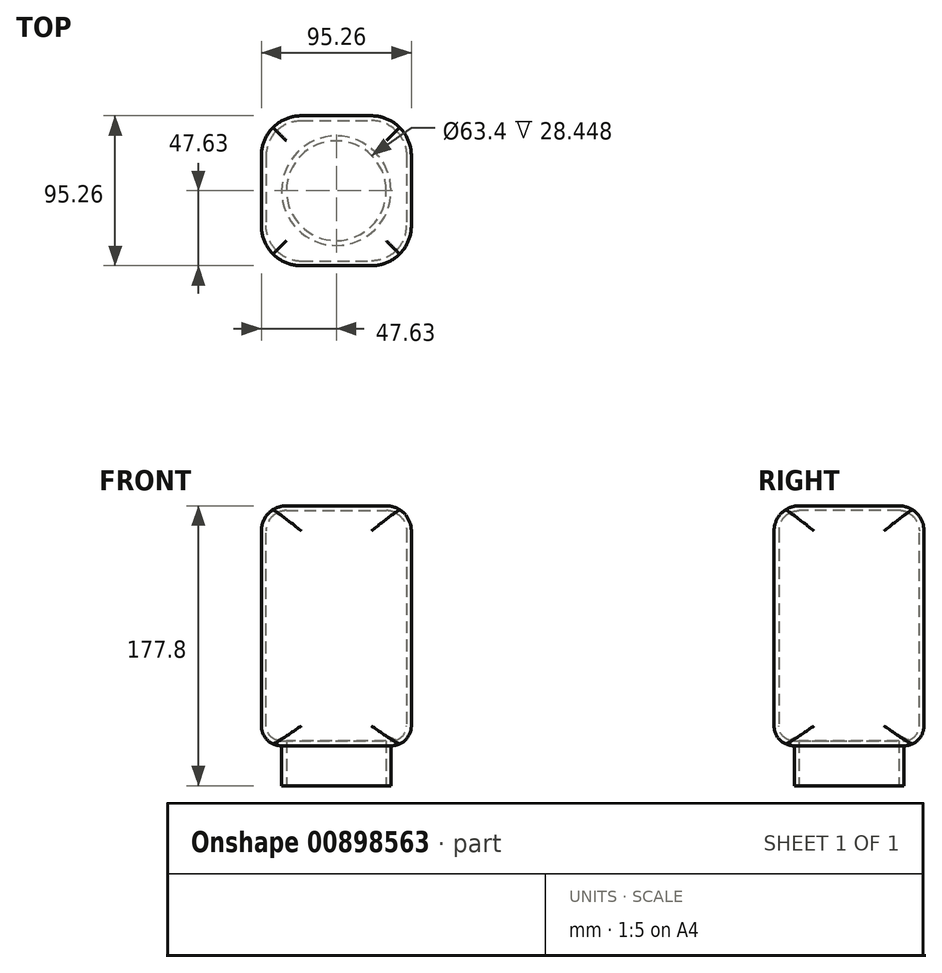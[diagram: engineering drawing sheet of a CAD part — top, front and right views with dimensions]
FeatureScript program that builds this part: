
annotation { "Feature Type Name" : "Feature", "Feature Type Description" : "" }
export const myFeature = defineFeature(function(context is Context, id is Id, definition is map)
    precondition{}
    {
        {
            var Q0;
            Q0=qCreatedBy(makeId("Front.planeOp"),FACE);
            var sketch = newSketch(context, id + "F0", { "sketchPlane" : qUnion([Q0])});
            skLineSegment(sketch, "E0", {"start": v(0, 0) * mm, "end": v(0, 110.8) * mm, "construction": true});
            skLineSegment(sketch, "E1", {"start": v(0, 0) * mm, "end": v(-34.75, 0) * mm});
            skLineSegment(sketch, "E2", {"start": v(-34.75, 0) * mm, "end": v(-34.75, -25.4) * mm});
            skLineSegment(sketch, "E3", {"start": v(-34.75, -25.4) * mm, "end": v(0, -25.4) * mm});
            skLineSegment(sketch, "E4", {"start": v(0, -25.4) * mm, "end": v(0, 0) * mm});
            skSolve(sketch);
        }
        {
            var Q0;
            Q0=makeQuery(id+"F0.imprint","IMPRINT",FACE,{"disambiguationData":[TD([[makeQuery(id+"F0.imprint","IMPRINT",EDGE,{"derivedFrom":sQuery(id+"F0.wireOp",EDGE,"E1")}),1.0]])]});
            var Q1;
            Q1=sQuery(id+"F0.wireOp",EDGE,"E0");
            revolve(context, id + "F1", {"surfaceOperationType" : NewSurfaceOperationType.NEW, "entities" : qUnion([Q0]), "axis" : qUnion([Q1]), "revolveType" : RevolveType.FULL});
        }
        {
            var Q0;
            Q0=qCreatedBy(makeId("Top.planeOp"),FACE);
            var sketch = newSketch(context, id + "F2", { "sketchPlane" : qUnion([Q0])});
            skLineSegment(sketch, "E5", {"start": v(-22.23, 47.63) * mm, "end": v(22.23, 47.63) * mm});
            skLineSegment(sketch, "E6", {"start": v(47.63, 22.23) * mm, "end": v(47.63, -22.23) * mm});
            skLineSegment(sketch, "E7", {"start": v(22.23, -47.63) * mm, "end": v(-22.22, -47.63) * mm});
            skLineSegment(sketch, "E8", {"start": v(-47.62, -22.23) * mm, "end": v(-47.62, 22.23) * mm});
            skPoint(sketch, "E9.visualSharp", {"position": v(-47.62, 47.63) * mm});
            skArc(sketch, "E9.filletArc", {"start": v(-22.23, 47.63) * mm, "mid": v(-40.19, 40.19) * mm, "end": v(-47.63, 22.23) * mm});
            skPoint(sketch, "E10.visualSharp", {"position": v(47.63, -47.63) * mm});
            skArc(sketch, "E10.filletArc", {"start": v(22.23, -47.63) * mm, "mid": v(40.19, -40.19) * mm, "end": v(47.63, -22.23) * mm});
            skPoint(sketch, "E11.visualSharp", {"position": v(47.62, 47.63) * mm});
            skArc(sketch, "E11.filletArc", {"start": v(47.62, 22.23) * mm, "mid": v(40.19, 40.19) * mm, "end": v(22.23, 47.62) * mm});
            skPoint(sketch, "E12.visualSharp", {"position": v(-47.62, -47.63) * mm});
            skArc(sketch, "E12.filletArc", {"start": v(-47.62, -22.23) * mm, "mid": v(-40.19, -40.19) * mm, "end": v(-22.22, -47.63) * mm});
            skSolve(sketch);
        }
        {
            var Q0;
            Q0=makeQuery(id+"F2.imprint","IMPRINT",FACE,{"disambiguationData":[TD([[makeQuery(id+"F2.imprint","IMPRINT",EDGE,{"derivedFrom":sQuery(id+"F2.wireOp",EDGE,"E5")}),-1.0]])]});
            extrude(context, id + "F3", {"entities" : qUnion([Q0]), "operationType" : NewBodyOperationType.ADD, "depth" : 152.4 * mm, "offsetDistance" : 25.4 * mm});
        }
        {
            var Q0;
            Q0=qCreatedBy(makeId("Front.planeOp"),FACE);
            var sketch = newSketch(context, id + "F4", { "sketchPlane" : qUnion([Q0])});
            skPoint(sketch, "E13.0", {"position": v(-47.62, 0) * mm});
            skPoint(sketch, "E14.0", {"position": v(-47.62, 152.4) * mm});
            skPoint(sketch, "E15.0", {"position": v(47.63, 0) * mm});
            skPoint(sketch, "E16.0", {"position": v(47.63, 152.4) * mm});
            skLineSegment(sketch, "E17", {"start": v(-47.62, 152.4) * mm, "end": v(-47.62, 141.05) * mm});
            skLineSegment(sketch, "E18", {"start": v(-47.62, 0) * mm, "end": v(-47.62, 12.7) * mm});
            skLineSegment(sketch, "E19", {"start": v(-47.62, 152.4) * mm, "end": v(-31.75, 152.4) * mm});
            skArc(sketch, "E20", {"start": v(-31.75, 152.4) * mm, "mid": v(-42.98, 147.75) * mm, "end": v(-47.63, 136.53) * mm});
            skArc(sketch, "E21", {"start": v(47.62, 136.53) * mm, "mid": v(42.98, 147.75) * mm, "end": v(31.75, 152.4) * mm});
            skArc(sketch, "E22", {"start": v(-47.62, 12.7) * mm, "mid": v(-43.9, 3.72) * mm, "end": v(-34.92, 0) * mm});
            skArc(sketch, "E23", {"start": v(34.93, 0) * mm, "mid": v(43.9, 3.72) * mm, "end": v(47.63, 12.7) * mm});
            skLineSegment(sketch, "E24", {"start": v(-47.62, 0) * mm, "end": v(-34.92, 0) * mm});
            skLineSegment(sketch, "E25", {"start": v(47.63, 152.4) * mm, "end": v(47.63, 136.53) * mm});
            skLineSegment(sketch, "E26", {"start": v(47.63, 152.4) * mm, "end": v(-31.75, 152.4) * mm});
            skLineSegment(sketch, "E27.trimOffspring", {"start": v(-47.62, 136.53) * mm, "end": v(-47.62, 152.4) * mm});
            skLineSegment(sketch, "E28.trimOffspring", {"start": v(47.63, 12.7) * mm, "end": v(47.63, 0) * mm});
            skLineSegment(sketch, "E29.trimOffspring", {"start": v(31.75, 152.4) * mm, "end": v(47.62, 152.4) * mm});
            skLineSegment(sketch, "E30.trimOffspring", {"start": v(34.92, 0) * mm, "end": v(47.62, 0) * mm});
            skSolve(sketch);
        }
        {
            var Q0;
            {var subQ0=sQuery(id+"F4.wireOp",EDGE,"E19");Q0=makeQuery(id+"F4.imprint","IMPRINT",FACE,{"disambiguationData":[TD([[makeQuery(id+"F4.imprint","IMPRINT",EDGE,{"derivedFrom":subQ0}),-1.0]])]});}
            var Q1;
            Q1=makeQuery(id+"F4.imprint","IMPRINT",FACE,{"disambiguationData":[TD([[makeQuery(id+"F4.imprint","IMPRINT",EDGE,{"derivedFrom":sQuery(id+"F4.wireOp",EDGE,"E21")}),-1.0]])]});
            var Q2;
            Q2=makeQuery(id+"F4.imprint","IMPRINT",FACE,{"disambiguationData":[TD([[makeQuery(id+"F4.imprint","IMPRINT",EDGE,{"derivedFrom":sQuery(id+"F4.wireOp",EDGE,"E18")}),-1.0]])]});
            var Q3;
            Q3=makeQuery(id+"F4.imprint","IMPRINT",FACE,{"disambiguationData":[TD([[makeQuery(id+"F4.imprint","IMPRINT",EDGE,{"derivedFrom":sQuery(id+"F4.wireOp",EDGE,"E23")}),-1.0]])]});
            extrude(context, id + "F5", {"entities" : qUnion([Q0, Q1, Q2, Q3]), "operationType" : NewBodyOperationType.REMOVE, "endBound" : BoundingType.SYMMETRIC, "oppositeDirection" : true, "depth" : 152.4 * mm, "offsetDistance" : 25.4 * mm});
        }
        {
            var Q0;
            Q0=qCreatedBy(makeId("Right.planeOp"),FACE);
            var sketch = newSketch(context, id + "F6", { "sketchPlane" : qUnion([Q0])});
            skPoint(sketch, "E31.0", {"position": v(-47.63, 152.4) * mm});
            skPoint(sketch, "E32.0", {"position": v(47.63, 152.4) * mm});
            skPoint(sketch, "E33.0", {"position": v(-47.63, 0) * mm});
            skPoint(sketch, "E34.0", {"position": v(47.63, 0) * mm});
            skLineSegment(sketch, "E35", {"start": v(-47.63, 152.4) * mm, "end": v(-31.75, 152.4) * mm});
            skLineSegment(sketch, "E36", {"start": v(47.63, 152.4) * mm, "end": v(47.63, 136.53) * mm});
            skLineSegment(sketch, "E37", {"start": v(47.63, 0) * mm, "end": v(34.93, 0) * mm});
            skLineSegment(sketch, "E38", {"start": v(-47.63, 0) * mm, "end": v(-47.63, 12.7) * mm});
            skArc(sketch, "E39", {"start": v(-31.75, 152.4) * mm, "mid": v(-42.98, 147.75) * mm, "end": v(-47.63, 136.53) * mm});
            skArc(sketch, "E40", {"start": v(47.63, 136.53) * mm, "mid": v(42.98, 147.75) * mm, "end": v(31.75, 152.4) * mm});
            skArc(sketch, "E41", {"start": v(-47.63, 12.7) * mm, "mid": v(-43.9, 3.72) * mm, "end": v(-34.93, 0) * mm});
            skArc(sketch, "E42", {"start": v(34.93, 0) * mm, "mid": v(43.9, 3.72) * mm, "end": v(47.63, 12.7) * mm});
            skLineSegment(sketch, "E43.trimOffspring", {"start": v(-47.63, 136.53) * mm, "end": v(-47.63, 152.4) * mm});
            skLineSegment(sketch, "E44.trimOffspring", {"start": v(31.75, 152.4) * mm, "end": v(47.63, 152.4) * mm});
            skLineSegment(sketch, "E45.trimOffspring", {"start": v(47.63, 12.7) * mm, "end": v(47.63, 0) * mm});
            skLineSegment(sketch, "E46.trimOffspring", {"start": v(-34.93, 0) * mm, "end": v(-47.63, 0) * mm});
            skSolve(sketch);
        }
        {
            var Q0;
            Q0=makeQuery(id+"F6.imprint","IMPRINT",FACE,{"disambiguationData":[TD([[makeQuery(id+"F6.imprint","IMPRINT",EDGE,{"derivedFrom":sQuery(id+"F6.wireOp",EDGE,"E35")}),-1.0]])]});
            var Q1;
            Q1=makeQuery(id+"F6.imprint","IMPRINT",FACE,{"disambiguationData":[TD([[makeQuery(id+"F6.imprint","IMPRINT",EDGE,{"derivedFrom":sQuery(id+"F6.wireOp",EDGE,"E38")}),-1.0]])]});
            var Q2;
            Q2=makeQuery(id+"F6.imprint","IMPRINT",FACE,{"disambiguationData":[TD([[makeQuery(id+"F6.imprint","IMPRINT",EDGE,{"derivedFrom":sQuery(id+"F6.wireOp",EDGE,"E36")}),-1.0]])]});
            var Q3;
            Q3=makeQuery(id+"F6.imprint","IMPRINT",FACE,{"disambiguationData":[TD([[makeQuery(id+"F6.imprint","IMPRINT",EDGE,{"derivedFrom":sQuery(id+"F6.wireOp",EDGE,"E37")}),-1.0]])]});
            extrude(context, id + "F7", {"entities" : qUnion([Q0, Q1, Q2, Q3]), "operationType" : NewBodyOperationType.REMOVE, "endBound" : BoundingType.SYMMETRIC, "oppositeDirection" : true, "depth" : 152.4 * mm, "offsetDistance" : 25.4 * mm});
        }
        {
            var Q0;
            Q0=makeQuery(id+"F1.opRevolve","SWEPT_FACE",FACE,{"disambiguationData":[OSD([sQuery(id+"F0.wireOp",EDGE,"E3")])]});
            shell(context, id + "F8", {"entities" : qUnion([Q0]), "thickness" : 3.05 * mm});
        }
    });
